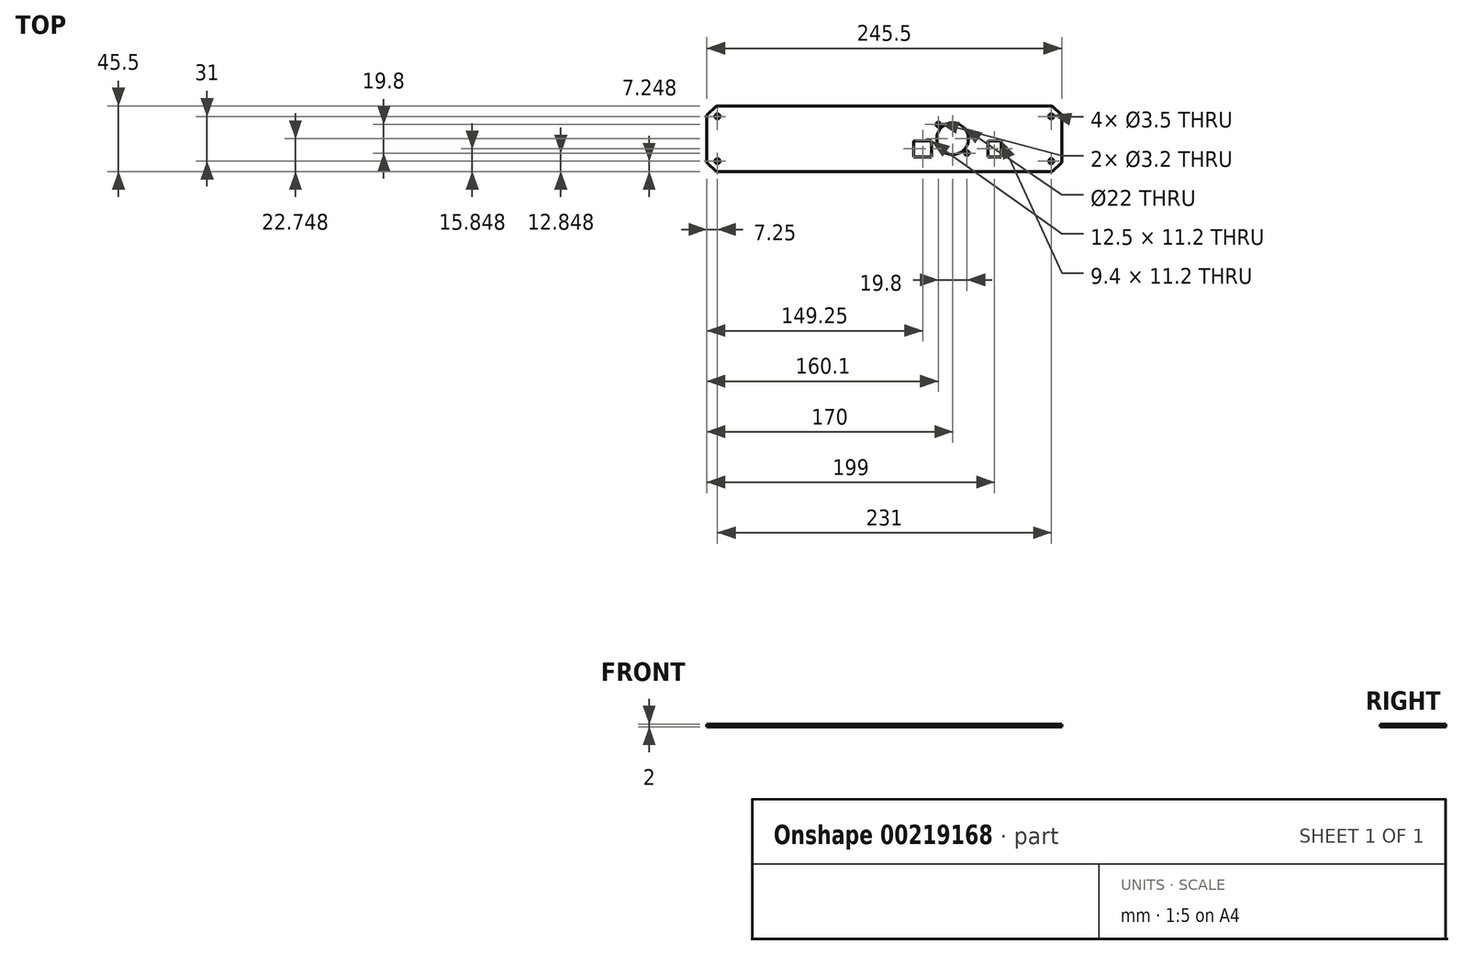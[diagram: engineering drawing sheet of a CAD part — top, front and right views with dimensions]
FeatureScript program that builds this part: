
annotation { "Feature Type Name" : "Feature", "Feature Type Description" : "" }
export const myFeature = defineFeature(function(context is Context, id is Id, definition is map)
    precondition{}
    {
        {
            var Q0;
            Q0=qCreatedBy(makeId("Top.planeOp"),FACE);
            var sketch = newSketch(context, id + "F0", { "sketchPlane" : qUnion([Q0])});
            skCircle(sketch, "E0.5.0.0", {"center": v(55.4, -2.07) * mm, "radius": 11 * mm});
            skCircle(sketch, "E0.5.0.1", {"center": v(45.5, 7.83) * mm, "radius": 1.6 * mm});
            skCircle(sketch, "E0.5.0.2", {"center": v(65.3, -11.97) * mm, "radius": 1.6 * mm});
            skLineSegment(sketch, "E1", {"start": v(-108.1, 20.68) * mm, "end": v(124.4, 20.68) * mm});
            skLineSegment(sketch, "E2", {"start": v(-114.6, 14.18) * mm, "end": v(-114.6, -18.32) * mm});
            skLineSegment(sketch, "E3", {"start": v(-108.1, -24.82) * mm, "end": v(124.4, -24.82) * mm});
            skLineSegment(sketch, "E4", {"start": v(130.9, 14.18) * mm, "end": v(130.9, -18.32) * mm});
            skLineSegment(sketch, "E5", {"start": v(-108.1, 20.68) * mm, "end": v(-114.6, 14.18) * mm});
            skLineSegment(sketch, "E6", {"start": v(-114.6, -18.32) * mm, "end": v(-108.1, -24.82) * mm});
            skLineSegment(sketch, "E7", {"start": v(130.9, -18.32) * mm, "end": v(124.4, -24.82) * mm});
            skLineSegment(sketch, "E8", {"start": v(130.9, 14.18) * mm, "end": v(124.4, 20.68) * mm});
            skPoint(sketch, "E9.left.start.orphan", {"position": v(-110.61, 20.68) * mm});
            skCircle(sketch, "E10", {"center": v(-107.36, 13.43) * mm, "radius": 1.75 * mm});
            skLineSegment(sketch, "E11.bottom", {"start": v(-107.36, 13.43) * mm, "end": v(123.64, 13.43) * mm, "construction": true});
            skLineSegment(sketch, "E11.top", {"start": v(-107.36, -17.57) * mm, "end": v(123.64, -17.57) * mm, "construction": true});
            skLineSegment(sketch, "E11.left", {"start": v(-107.36, 13.43) * mm, "end": v(-107.36, -17.57) * mm, "construction": true});
            skLineSegment(sketch, "E11.right", {"start": v(123.64, 13.43) * mm, "end": v(123.64, -17.57) * mm, "construction": true});
            skCircle(sketch, "E12", {"center": v(-107.36, -17.57) * mm, "radius": 1.75 * mm});
            skCircle(sketch, "E13", {"center": v(123.64, 13.43) * mm, "radius": 1.75 * mm});
            skCircle(sketch, "E14", {"center": v(123.64, -17.57) * mm, "radius": 1.75 * mm});
            skLineSegment(sketch, "E15", {"start": v(-91.36, 128.78) * mm, "end": v(139.64, 128.78) * mm});
            skLineSegment(sketch, "E16", {"start": v(139.64, 128.78) * mm, "end": v(146.9, 121.53) * mm});
            skLineSegment(sketch, "E17", {"start": v(146.9, 121.53) * mm, "end": v(146.9, 90.53) * mm});
            skLineSegment(sketch, "E18", {"start": v(146.9, 90.53) * mm, "end": v(139.64, 83.28) * mm});
            skLineSegment(sketch, "E19", {"start": v(139.64, 83.28) * mm, "end": v(-91.36, 83.28) * mm});
            skLineSegment(sketch, "E20", {"start": v(-91.36, 83.28) * mm, "end": v(-98.6, 90.53) * mm});
            skLineSegment(sketch, "E21", {"start": v(-98.6, 90.53) * mm, "end": v(-98.6, 121.53) * mm});
            skLineSegment(sketch, "E22", {"start": v(-98.6, 121.53) * mm, "end": v(-91.36, 128.78) * mm});
            skLineSegment(sketch, "E23", {"start": v(-9.01, -14.57) * mm, "end": v(76.1, -14.57) * mm, "construction": true});
            skLineSegment(sketch, "E24.bottom", {"start": v(28.4, -14.57) * mm, "end": v(40.9, -14.57) * mm});
            skLineSegment(sketch, "E24.top", {"start": v(28.4, -3.37) * mm, "end": v(40.9, -3.37) * mm});
            skLineSegment(sketch, "E24.left", {"start": v(28.4, -14.57) * mm, "end": v(28.4, -3.37) * mm});
            skLineSegment(sketch, "E24.right", {"start": v(40.9, -14.57) * mm, "end": v(40.9, -3.37) * mm});
            skLineSegment(sketch, "E25.bottom", {"start": v(79.7, -14.57) * mm, "end": v(89.1, -14.57) * mm});
            skLineSegment(sketch, "E25.top", {"start": v(79.7, -3.37) * mm, "end": v(89.1, -3.37) * mm});
            skLineSegment(sketch, "E25.left", {"start": v(79.7, -14.57) * mm, "end": v(79.7, -3.37) * mm});
            skLineSegment(sketch, "E25.right", {"start": v(89.1, -14.57) * mm, "end": v(89.1, -3.37) * mm});
            skSolve(sketch);
        }
        {
            var Q0;
            Q0=makeQuery(id+"F0.imprint","IMPRINT",FACE,{"disambiguationData":[TD([[makeQuery(id+"F0.imprint","IMPRINT",EDGE,{"derivedFrom":sQuery(id+"F0.wireOp",EDGE,"E0.5.0.0")}),-1.0]])]});
            extrude(context, id + "F1", {"entities" : qUnion([Q0]), "depth" : 2 * mm});
        }
    });
